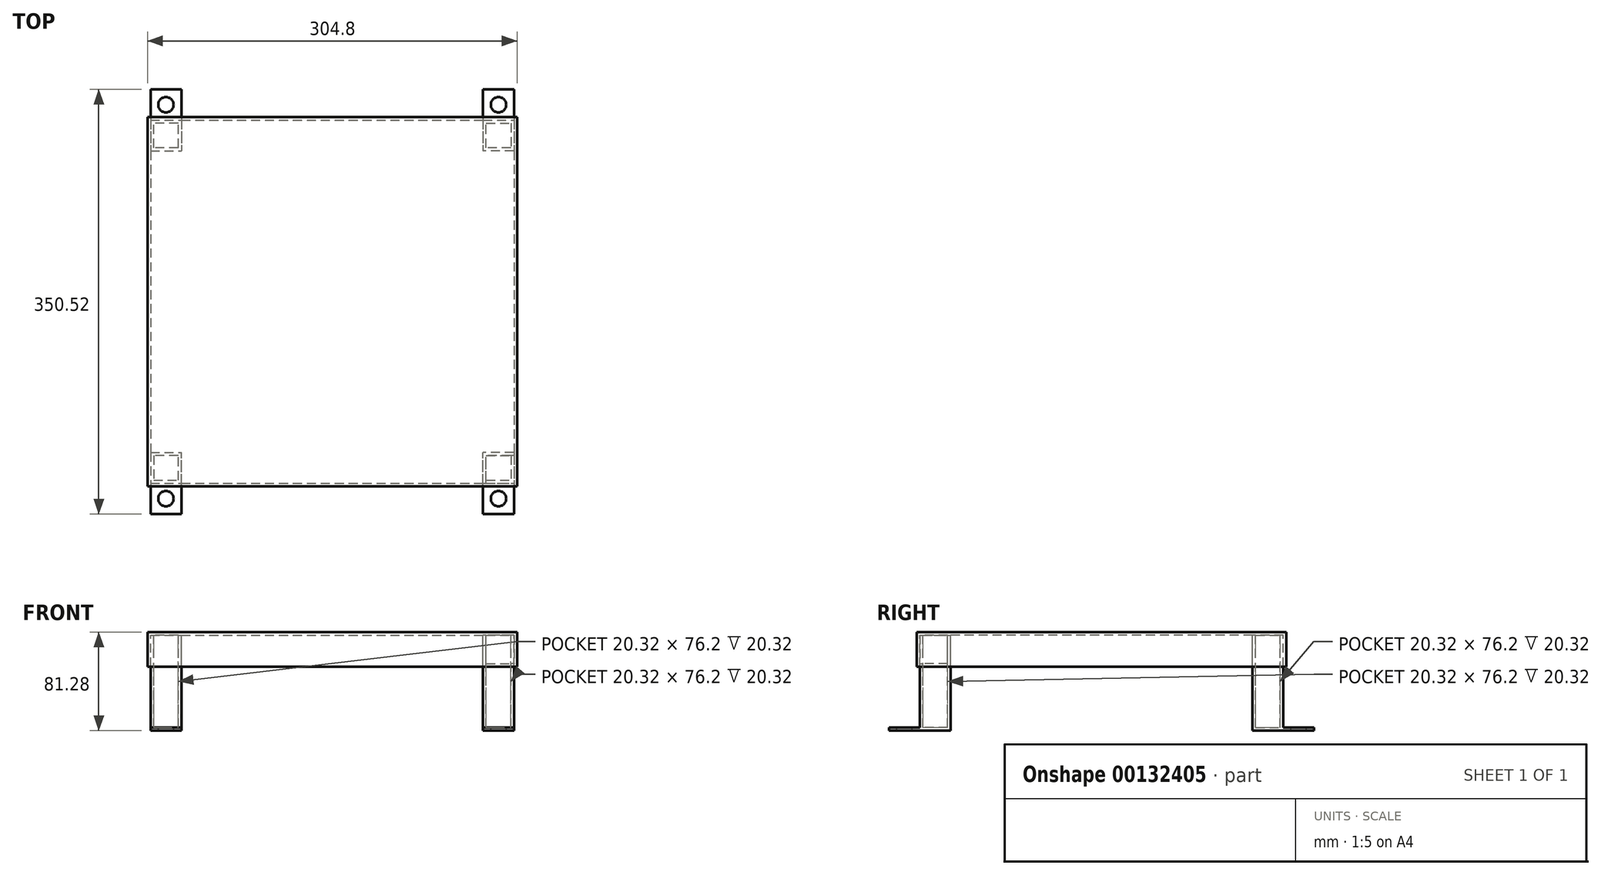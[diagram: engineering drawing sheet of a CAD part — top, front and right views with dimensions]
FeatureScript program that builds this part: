
annotation { "Feature Type Name" : "Feature", "Feature Type Description" : "" }
export const myFeature = defineFeature(function(context is Context, id is Id, definition is map)
    precondition{}
    {
        {
            var Q0;
            Q0=qCreatedBy(makeId("Top.planeOp"),FACE);
            var sketch = newSketch(context, id + "F0", { "sketchPlane" : qUnion([Q0])});
            skLineSegment(sketch, "E0.bottom", {"start": v(0, 0) * mm, "end": v(304.8, 0) * mm});
            skLineSegment(sketch, "E0.top", {"start": v(0, -304.8) * mm, "end": v(304.8, -304.8) * mm});
            skLineSegment(sketch, "E0.left", {"start": v(0, 0) * mm, "end": v(0, -304.8) * mm});
            skLineSegment(sketch, "E0.right", {"start": v(304.8, 0) * mm, "end": v(304.8, -304.8) * mm});
            skSolve(sketch);
        }
        {
            var Q0;
            Q0 = qSketchRegion(id + "F0", true);
            extrude(context, id + "F1", {"entities" : qUnion([Q0]), "depth" : 3 * mm});
        }
        {
            var Q0;
            Q0=makeQuery(id+"F1.opExtrude","CAP_FACE",FACE,{"disambiguationData":[OSD([sQuery(id+"F0.wireOp",EDGE,"E0.bottom"),sQuery(id+"F0.wireOp",EDGE,"E0.top"),sQuery(id+"F0.wireOp",EDGE,"E0.left"),sQuery(id+"F0.wireOp",EDGE,"E0.right")])],"isStart":true});
            var sketch = newSketch(context, id + "F2", { "sketchPlane" : qUnion([Q0])});
            skLineSegment(sketch, "E1.bottom", {"start": v(0, 0) * mm, "end": v(304.8, 0) * mm});
            skLineSegment(sketch, "E1.top", {"start": v(0, 304.8) * mm, "end": v(304.8, 304.8) * mm});
            skLineSegment(sketch, "E1.left", {"start": v(0, 0) * mm, "end": v(0, 304.8) * mm});
            skLineSegment(sketch, "E1.right", {"start": v(304.8, 0) * mm, "end": v(304.8, 304.8) * mm});
            skSolve(sketch);
        }
        {
            var Q0;
            Q0 = qSketchRegion(id + "F2", true);
            extrude(context, id + "F3", {"entities" : qUnion([Q0]), "operationType" : NewBodyOperationType.ADD, "depth" : 25.4 * mm});
        }
        {
            var Q0;
            Q0=makeQuery(id+"F3.opExtrude","CAP_FACE",FACE,{"disambiguationData":[OSD([sQuery(id+"F2.wireOp",EDGE,"E1.bottom"),sQuery(id+"F2.wireOp",EDGE,"E1.top"),sQuery(id+"F2.wireOp",EDGE,"E1.left"),sQuery(id+"F2.wireOp",EDGE,"E1.right")])],"isStart":false});
            shell(context, id + "F4", {"entities" : qUnion([Q0]), "thickness" : 2.54 * mm});
        }
        {
            var Q0;
            Q0=makeQuery(id+"F4.opShell","OFFSET_FACE",FACE,{"disambiguationData":[OSD([sQuery(id+"F0.wireOp",EDGE,"E0.bottom"),sQuery(id+"F0.wireOp",EDGE,"E0.top"),sQuery(id+"F0.wireOp",EDGE,"E0.left"),sQuery(id+"F0.wireOp",EDGE,"E0.right")])]});
            var sketch = newSketch(context, id + "F5", { "sketchPlane" : qUnion([Q0])});
            skLineSegment(sketch, "E2.bottom", {"start": v(302.26, 302.26) * mm, "end": v(276.86, 302.26) * mm});
            skLineSegment(sketch, "E2.top", {"start": v(302.26, 276.86) * mm, "end": v(276.86, 276.86) * mm});
            skLineSegment(sketch, "E2.left", {"start": v(302.26, 302.26) * mm, "end": v(302.26, 276.86) * mm});
            skLineSegment(sketch, "E2.right", {"start": v(276.86, 302.26) * mm, "end": v(276.86, 276.86) * mm});
            skSolve(sketch);
        }
        {
            var Q0;
            Q0 = qSketchRegion(id + "F5", true);
            extrude(context, id + "F6", {"entities" : qUnion([Q0]), "operationType" : NewBodyOperationType.ADD, "depth" : 76.2 * mm});
        }
        {
            var Q0;
            Q0=makeQuery(id+"F6.opExtrude","CAP_FACE",FACE,{"disambiguationData":[OSD([sQuery(id+"F5.wireOp",EDGE,"E2.bottom"),sQuery(id+"F5.wireOp",EDGE,"E2.top"),sQuery(id+"F5.wireOp",EDGE,"E2.left"),sQuery(id+"F5.wireOp",EDGE,"E2.right")])],"isStart":false});
            shell(context, id + "F7", {"entities" : qUnion([Q0]), "thickness" : 2.54 * mm});
        }
        {
            var Q0;
            Q0=makeQuery(id+"F4.opShell","OFFSET_FACE",FACE,{"disambiguationData":[OSD([sQuery(id+"F0.wireOp",EDGE,"E0.bottom"),sQuery(id+"F0.wireOp",EDGE,"E0.top"),sQuery(id+"F0.wireOp",EDGE,"E0.left"),sQuery(id+"F0.wireOp",EDGE,"E0.right")])]});
            var sketch = newSketch(context, id + "F8", { "sketchPlane" : qUnion([Q0])});
            skLineSegment(sketch, "E3.bottom", {"start": v(2.54, 2.54) * mm, "end": v(27.94, 2.54) * mm});
            skLineSegment(sketch, "E3.top", {"start": v(2.54, 27.94) * mm, "end": v(27.94, 27.94) * mm});
            skLineSegment(sketch, "E3.left", {"start": v(2.54, 2.54) * mm, "end": v(2.54, 27.94) * mm});
            skLineSegment(sketch, "E3.right", {"start": v(27.94, 2.54) * mm, "end": v(27.94, 27.94) * mm});
            skLineSegment(sketch, "E4.bottom", {"start": v(302.26, 2.54) * mm, "end": v(276.86, 2.54) * mm});
            skLineSegment(sketch, "E4.top", {"start": v(302.26, 27.94) * mm, "end": v(276.86, 27.94) * mm});
            skLineSegment(sketch, "E4.left", {"start": v(302.26, 2.54) * mm, "end": v(302.26, 27.94) * mm});
            skLineSegment(sketch, "E4.right", {"start": v(276.86, 2.54) * mm, "end": v(276.86, 27.94) * mm});
            skLineSegment(sketch, "E5.bottom", {"start": v(2.54, 302.26) * mm, "end": v(27.94, 302.26) * mm});
            skLineSegment(sketch, "E5.top", {"start": v(2.54, 276.86) * mm, "end": v(27.94, 276.86) * mm});
            skLineSegment(sketch, "E5.left", {"start": v(2.54, 302.26) * mm, "end": v(2.54, 276.86) * mm});
            skLineSegment(sketch, "E5.right", {"start": v(27.94, 302.26) * mm, "end": v(27.94, 276.86) * mm});
            skLineSegment(sketch, "E6.bottom", {"start": v(25.4, 25.4) * mm, "end": v(5.08, 25.4) * mm});
            skLineSegment(sketch, "E6.top", {"start": v(25.4, 5.08) * mm, "end": v(5.08, 5.08) * mm});
            skLineSegment(sketch, "E6.left", {"start": v(25.4, 25.4) * mm, "end": v(25.4, 5.08) * mm});
            skLineSegment(sketch, "E6.right", {"start": v(5.08, 25.4) * mm, "end": v(5.08, 5.08) * mm});
            skLineSegment(sketch, "E7", {"start": v(15.24, 279.4) * mm, "end": v(5.08, 279.4) * mm});
            skLineSegment(sketch, "E8", {"start": v(5.08, 279.4) * mm, "end": v(5.08, 299.72) * mm});
            skLineSegment(sketch, "E9", {"start": v(5.08, 299.72) * mm, "end": v(25.4, 299.72) * mm});
            skLineSegment(sketch, "E10", {"start": v(25.4, 299.72) * mm, "end": v(25.4, 279.4) * mm});
            skLineSegment(sketch, "E11", {"start": v(25.4, 279.4) * mm, "end": v(15.24, 279.4) * mm});
            skPoint(sketch, "E12.endSnap0", {"position": v(276.86, 15.24) * mm});
            skPoint(sketch, "E13.endSnap0", {"position": v(302.26, 15.24) * mm});
            skLineSegment(sketch, "E14", {"start": v(279.4, 15.24) * mm, "end": v(279.4, 5.08) * mm});
            skLineSegment(sketch, "E15", {"start": v(279.4, 5.08) * mm, "end": v(299.72, 5.08) * mm});
            skLineSegment(sketch, "E16", {"start": v(299.72, 5.08) * mm, "end": v(299.72, 25.4) * mm});
            skLineSegment(sketch, "E17", {"start": v(299.72, 25.4) * mm, "end": v(279.4, 25.4) * mm});
            skLineSegment(sketch, "E18", {"start": v(279.4, 25.4) * mm, "end": v(279.4, 15.24) * mm});
            skSolve(sketch);
        }
        {
            var Q0;
            Q0 = qSketchRegion(id + "F8", true);
            extrude(context, id + "F9", {"entities" : qUnion([Q0]), "operationType" : NewBodyOperationType.ADD, "depth" : 76.2 * mm});
        }
        {
            var Q0;
            Q0=makeQuery(id+"F9.opExtrude","CAP_FACE",FACE,{"disambiguationData":[OSD([sQuery(id+"F8.wireOp",EDGE,"E4.bottom"),sQuery(id+"F8.wireOp",EDGE,"E4.top"),sQuery(id+"F8.wireOp",EDGE,"E4.left"),sQuery(id+"F8.wireOp",EDGE,"E4.right"),sQuery(id+"F8.wireOp",EDGE,"E14"),sQuery(id+"F8.wireOp",EDGE,"E15"),sQuery(id+"F8.wireOp",EDGE,"E16"),sQuery(id+"F8.wireOp",EDGE,"E17"),sQuery(id+"F8.wireOp",EDGE,"E18")])],"isStart":false});
            var sketch = newSketch(context, id + "F10", { "sketchPlane" : qUnion([Q0])});
            skLineSegment(sketch, "E19.bottom", {"start": v(302.26, 27.94) * mm, "end": v(276.86, 27.94) * mm});
            skLineSegment(sketch, "E19.top", {"start": v(302.26, -22.86) * mm, "end": v(276.86, -22.86) * mm});
            skLineSegment(sketch, "E19.left", {"start": v(302.26, 27.94) * mm, "end": v(302.26, -22.86) * mm});
            skLineSegment(sketch, "E19.right", {"start": v(276.86, 27.94) * mm, "end": v(276.86, -22.86) * mm});
            skCircle(sketch, "E20", {"center": v(289.56, -10.16) * mm, "radius": 6.35 * mm});
            skSolve(sketch);
        }
        {
            var Q0;
            Q0 = qSketchRegion(id + "F10", true);
            extrude(context, id + "F11", {"entities" : qUnion([Q0]), "operationType" : NewBodyOperationType.ADD, "depth" : 2.54 * mm});
        }
        {
            var Q0;
            Q0=makeQuery(id+"F9.opExtrude","CAP_FACE",FACE,{"disambiguationData":[OSD([sQuery(id+"F8.wireOp",EDGE,"E3.bottom"),sQuery(id+"F8.wireOp",EDGE,"E3.top"),sQuery(id+"F8.wireOp",EDGE,"E3.left"),sQuery(id+"F8.wireOp",EDGE,"E3.right"),sQuery(id+"F8.wireOp",EDGE,"E6.bottom"),sQuery(id+"F8.wireOp",EDGE,"E6.top"),sQuery(id+"F8.wireOp",EDGE,"E6.left"),sQuery(id+"F8.wireOp",EDGE,"E6.right")])],"isStart":false});
            var sketch = newSketch(context, id + "F12", { "sketchPlane" : qUnion([Q0])});
            skLineSegment(sketch, "E21.bottom", {"start": v(27.94, 27.94) * mm, "end": v(2.54, 27.94) * mm});
            skLineSegment(sketch, "E21.top", {"start": v(27.94, -22.86) * mm, "end": v(2.54, -22.86) * mm});
            skLineSegment(sketch, "E21.left", {"start": v(27.94, 27.94) * mm, "end": v(27.94, -22.86) * mm});
            skLineSegment(sketch, "E21.right", {"start": v(2.54, 27.94) * mm, "end": v(2.54, -22.86) * mm});
            skCircle(sketch, "E22", {"center": v(15.24, -10.16) * mm, "radius": 6.35 * mm});
            skSolve(sketch);
        }
        {
            var Q0;
            Q0 = qSketchRegion(id + "F12", true);
            extrude(context, id + "F13", {"entities" : qUnion([Q0]), "operationType" : NewBodyOperationType.ADD, "depth" : 2.54 * mm});
        }
        {
            var Q0;
            Q0=makeQuery(id+"F9.opExtrude","CAP_FACE",FACE,{"disambiguationData":[OSD([sQuery(id+"F8.wireOp",EDGE,"E5.bottom"),sQuery(id+"F8.wireOp",EDGE,"E5.top"),sQuery(id+"F8.wireOp",EDGE,"E5.left"),sQuery(id+"F8.wireOp",EDGE,"E5.right"),sQuery(id+"F8.wireOp",EDGE,"E7"),sQuery(id+"F8.wireOp",EDGE,"E8"),sQuery(id+"F8.wireOp",EDGE,"E9"),sQuery(id+"F8.wireOp",EDGE,"E10"),sQuery(id+"F8.wireOp",EDGE,"E11")])],"isStart":false});
            var sketch = newSketch(context, id + "F14", { "sketchPlane" : qUnion([Q0])});
            skLineSegment(sketch, "E23.bottom", {"start": v(27.94, 276.86) * mm, "end": v(2.54, 276.86) * mm});
            skLineSegment(sketch, "E23.top", {"start": v(27.94, 327.66) * mm, "end": v(2.54, 327.66) * mm});
            skLineSegment(sketch, "E23.left", {"start": v(27.94, 276.86) * mm, "end": v(27.94, 327.66) * mm});
            skLineSegment(sketch, "E23.right", {"start": v(2.54, 276.86) * mm, "end": v(2.54, 327.66) * mm});
            skCircle(sketch, "E24", {"center": v(15.24, 314.96) * mm, "radius": 6.35 * mm});
            skSolve(sketch);
        }
        {
            var Q0;
            Q0 = qSketchRegion(id + "F14", true);
            extrude(context, id + "F15", {"entities" : qUnion([Q0]), "operationType" : NewBodyOperationType.ADD, "depth" : 2.54 * mm});
        }
        {
            var Q0;
            Q0=makeQuery(id+"F6.opExtrude","CAP_FACE",FACE,{"disambiguationData":[OSD([sQuery(id+"F5.wireOp",EDGE,"E2.bottom"),sQuery(id+"F5.wireOp",EDGE,"E2.top"),sQuery(id+"F5.wireOp",EDGE,"E2.left"),sQuery(id+"F5.wireOp",EDGE,"E2.right")])],"isStart":false});
            var sketch = newSketch(context, id + "F16", { "sketchPlane" : qUnion([Q0])});
            skPoint(sketch, "E25.oppositeSnap0", {"position": v(302.26, 289.56) * mm});
            skLineSegment(sketch, "E25.bottom", {"start": v(276.86, 276.86) * mm, "end": v(302.26, 276.86) * mm});
            skLineSegment(sketch, "E25.top", {"start": v(276.86, 327.66) * mm, "end": v(302.26, 327.66) * mm});
            skLineSegment(sketch, "E25.left", {"start": v(276.86, 276.86) * mm, "end": v(276.86, 327.66) * mm});
            skLineSegment(sketch, "E25.right", {"start": v(302.26, 276.86) * mm, "end": v(302.26, 327.66) * mm});
            skCircle(sketch, "E26", {"center": v(289.56, 314.96) * mm, "radius": 6.35 * mm});
            skSolve(sketch);
        }
        {
            var Q0;
            Q0 = qSketchRegion(id + "F16", true);
            extrude(context, id + "F17", {"entities" : qUnion([Q0]), "operationType" : NewBodyOperationType.ADD, "depth" : 2.54 * mm});
        }
    });
